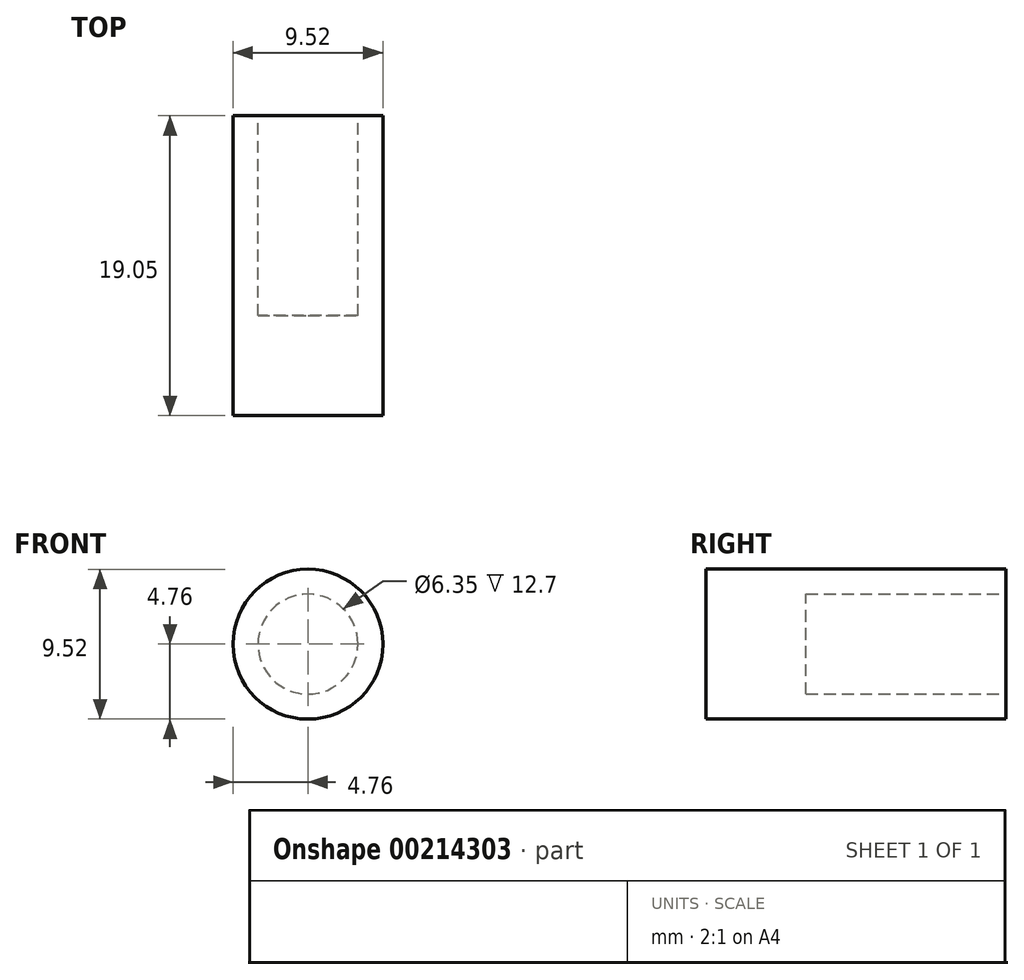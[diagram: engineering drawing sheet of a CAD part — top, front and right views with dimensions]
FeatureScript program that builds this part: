
annotation { "Feature Type Name" : "Feature", "Feature Type Description" : "" }
export const myFeature = defineFeature(function(context is Context, id is Id, definition is map)
    precondition{}
    {
        {
            var Q0;
            Q0=qCreatedBy(makeId("Front.planeOp"),FACE);
            var sketch = newSketch(context, id + "F0", { "sketchPlane" : qUnion([Q0])});
            skCircle(sketch, "E0", {"center": v(0, 0) * mm, "radius": 4.76 * mm});
            skCircle(sketch, "E1", {"center": v(0, 0) * mm, "radius": 3.18 * mm});
            skSolve(sketch);
        }
        {
            var Q0;
            Q0 = qSketchRegion(id + "F0", true);
            var Q1;
            Q1=makeQuery(id+"F0.imprint","IMPRINT",FACE,{"disambiguationData":[TD([[makeQuery(id+"F0.imprint","IMPRINT",EDGE,{"derivedFrom":sQuery(id+"F0.wireOp",EDGE,"E1")}),1.0]])]});
            extrude(context, id + "F1", {"entities" : qUnion([Q0, Q1]), "depth" : 19.05 * mm});
        }
        {
            var Q0;
            Q0=makeQuery(id+"F0.imprint","IMPRINT",FACE,{"disambiguationData":[TD([[makeQuery(id+"F0.imprint","IMPRINT",EDGE,{"derivedFrom":sQuery(id+"F0.wireOp",EDGE,"E1")}),1.0]])]});
            extrude(context, id + "F2", {"entities" : qUnion([Q0]), "operationType" : NewBodyOperationType.REMOVE, "depth" : 12.7 * mm});
        }
    });
